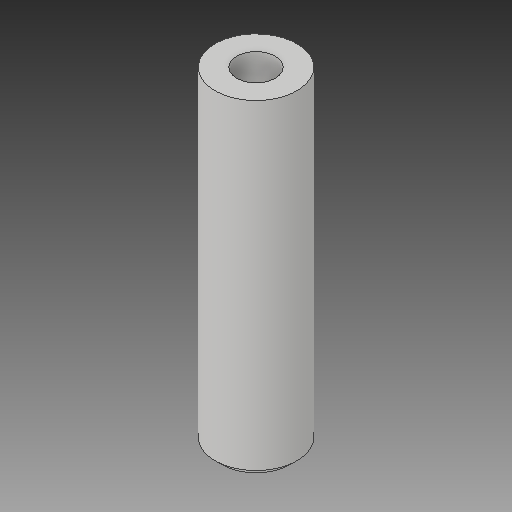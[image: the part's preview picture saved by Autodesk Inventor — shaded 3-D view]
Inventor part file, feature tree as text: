
AUTODESK INVENTOR PART (.ipt)
format: ipt  version: 2018 (Build 220112000, 112)  size: 98,304 bytes
history: native  units: mm
features: extrude x1, chamfer x1, sketch x1
ambient origin geometry x8: Origin, YZ Plane, XZ Plane, XY Plane, X Axis, Y Axis, Z Axis, Center Point
bodies: Solid1 (feature_tree)
feature tree (3):
  extrude  "Extrusion1"  Depth=2.0mm
  chamfer  "Chamfer1"  Distance=200.0mm
  sketch  "Sketch1"  dims[d0=50.0mm d1=23.5mm d2=200.0mm d3=0.0mm d4=4.0mm d5=2.0mm d6=45.0deg]
